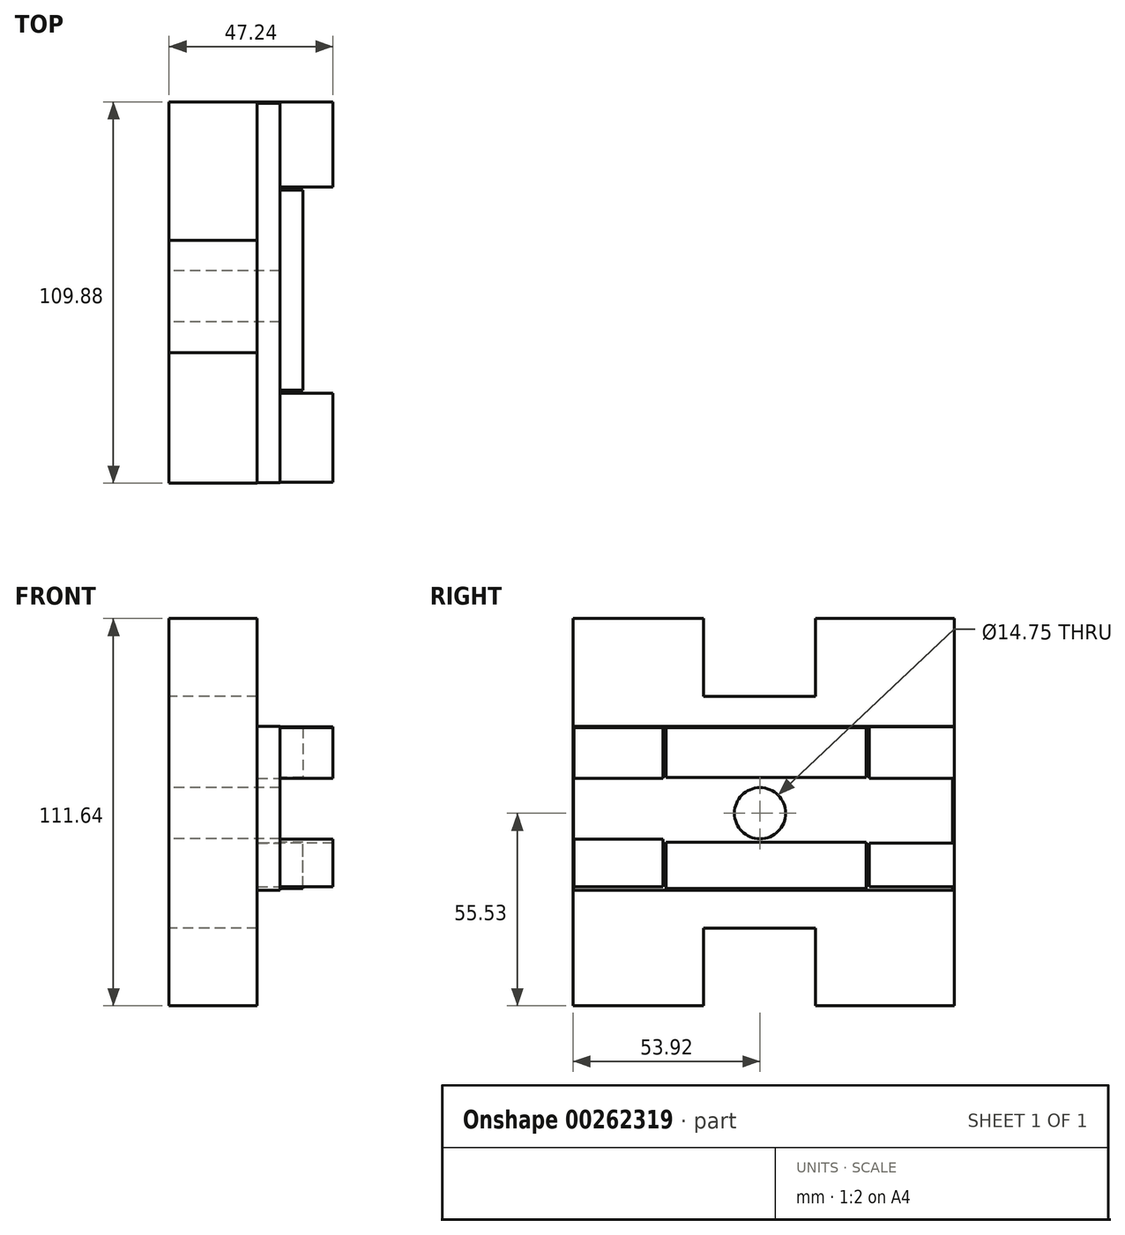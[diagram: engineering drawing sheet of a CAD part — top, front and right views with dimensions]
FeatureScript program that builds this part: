
annotation { "Feature Type Name" : "Feature", "Feature Type Description" : "" }
export const myFeature = defineFeature(function(context is Context, id is Id, definition is map)
    precondition{}
    {
        {
            var Q0;
            Q0=qCreatedBy(makeId("Right.planeOp"),FACE);
            var sketch = newSketch(context, id + "F0", { "sketchPlane" : qUnion([Q0])});
            skLineSegment(sketch, "E0.bottom", {"start": v(-53.92, 56.1) * mm, "end": v(55.96, 56.1) * mm});
            skLineSegment(sketch, "E0.top", {"start": v(-53.92, -55.53) * mm, "end": v(55.96, -55.53) * mm});
            skLineSegment(sketch, "E0.left", {"start": v(-53.92, 56.1) * mm, "end": v(-53.92, -55.53) * mm});
            skLineSegment(sketch, "E0.right", {"start": v(55.96, 56.1) * mm, "end": v(55.96, -55.53) * mm});
            skLineSegment(sketch, "E1.bottom", {"start": v(-16.32, 56.1) * mm, "end": v(16.03, 56.1) * mm});
            skLineSegment(sketch, "E1.top", {"start": v(-16.32, 33.67) * mm, "end": v(16.03, 33.67) * mm});
            skLineSegment(sketch, "E1.left", {"start": v(-16.32, 56.1) * mm, "end": v(-16.32, 33.67) * mm});
            skLineSegment(sketch, "E1.right", {"start": v(16.03, 56.1) * mm, "end": v(16.03, 33.67) * mm});
            skLineSegment(sketch, "E2.bottom", {"start": v(-16.32, -55.53) * mm, "end": v(16.03, -55.53) * mm});
            skLineSegment(sketch, "E2.top", {"start": v(-16.32, -33.08) * mm, "end": v(16.03, -33.08) * mm});
            skLineSegment(sketch, "E2.left", {"start": v(-16.32, -55.53) * mm, "end": v(-16.32, -33.08) * mm});
            skLineSegment(sketch, "E2.right", {"start": v(16.03, -55.53) * mm, "end": v(16.03, -33.08) * mm});
            skSolve(sketch);
        }
        {
            var Q0;
            {var subQ0=sQuery(id+"F0.wireOp",EDGE,"E0.left");Q0=makeQuery(id+"F0.imprint","IMPRINT",FACE,{"disambiguationData":[TD([[makeQuery(id+"F0.imprint","IMPRINT",EDGE,{"derivedFrom":subQ0}),1.0]])]});}
            extrude(context, id + "F1", {"entities" : qUnion([Q0]), "depth" : 25.4 * mm});
        }
        {
            var Q0;
            Q0=qCreatedBy(makeId("Right.planeOp"),FACE);
            var sketch = newSketch(context, id + "F2", { "sketchPlane" : qUnion([Q0])});
            skLineSegment(sketch, "E3", {"start": v(55.53, 25.07) * mm, "end": v(-53.78, 25.07) * mm});
            skLineSegment(sketch, "E4", {"start": v(-53.78, 25.07) * mm, "end": v(-53.78, -22.15) * mm});
            skLineSegment(sketch, "E5", {"start": v(-53.78, -22.15) * mm, "end": v(55.53, -22.15) * mm});
            skLineSegment(sketch, "E6", {"start": v(55.53, -22.15) * mm, "end": v(55.53, 25.07) * mm});
            skSolve(sketch);
        }
        {
            var Q0;
            Q0 = qSketchRegion(id + "F2", true);
            extrude(context, id + "F3", {"entities" : qUnion([Q0]), "operationType" : NewBodyOperationType.ADD, "depth" : 32 * mm});
        }
        {
            var Q0;
            Q0=qCreatedBy(makeId("Right.planeOp"),FACE);
            var sketch = newSketch(context, id + "F4", { "sketchPlane" : qUnion([Q0])});
            skLineSegment(sketch, "E7", {"start": v(-53.63, 10.06) * mm, "end": v(-27.98, 10.06) * mm});
            skLineSegment(sketch, "E8", {"start": v(-27.98, 24.63) * mm, "end": v(-27.98, 10.06) * mm});
            skLineSegment(sketch, "E9", {"start": v(-53.63, -21.13) * mm, "end": v(-53.63, -7.43) * mm});
            skLineSegment(sketch, "E10", {"start": v(-53.63, -7.43) * mm, "end": v(-27.98, -7.43) * mm});
            skLineSegment(sketch, "E11", {"start": v(-27.98, -7.43) * mm, "end": v(-27.98, -21.13) * mm});
            skLineSegment(sketch, "E12", {"start": v(-27.98, -21.13) * mm, "end": v(-53.63, -21.13) * mm});
            skLineSegment(sketch, "E13", {"start": v(-53.63, -7.43) * mm, "end": v(-53.63, -21.13) * mm});
            skLineSegment(sketch, "E14", {"start": v(-53.63, 10.06) * mm, "end": v(-53.63, 24.63) * mm});
            skLineSegment(sketch, "E15", {"start": v(-53.63, 24.63) * mm, "end": v(-27.98, 24.63) * mm});
            skLineSegment(sketch, "E16.bottom", {"start": v(55.67, 10.06) * mm, "end": v(31.48, 10.06) * mm});
            skLineSegment(sketch, "E16.top", {"start": v(55.67, 10.06) * mm, "end": v(31.48, 10.06) * mm});
            skLineSegment(sketch, "E16.left", {"start": v(55.67, 10.06) * mm, "end": v(55.67, 10.06) * mm});
            skLineSegment(sketch, "E16.right", {"start": v(31.48, 10.06) * mm, "end": v(31.48, 10.06) * mm});
            skLineSegment(sketch, "E17.bottom", {"start": v(31.48, 24.92) * mm, "end": v(31.48, 24.92) * mm});
            skLineSegment(sketch, "E17.left", {"start": v(31.48, 24.92) * mm, "end": v(31.48, 10.06) * mm});
            skLineSegment(sketch, "E17.right", {"start": v(31.48, 24.92) * mm, "end": v(31.48, 10.06) * mm});
            skLineSegment(sketch, "E18.bottom", {"start": v(31.48, 24.92) * mm, "end": v(55.96, 24.92) * mm});
            skLineSegment(sketch, "E18.top", {"start": v(31.48, 24.92) * mm, "end": v(55.96, 24.92) * mm});
            skLineSegment(sketch, "E18.right", {"start": v(55.96, 24.92) * mm, "end": v(55.96, 24.92) * mm});
            skLineSegment(sketch, "E19.bottom", {"start": v(55.67, 10.06) * mm, "end": v(55.96, 10.06) * mm});
            skLineSegment(sketch, "E19.top", {"start": v(55.67, 24.92) * mm, "end": v(55.96, 24.92) * mm});
            skLineSegment(sketch, "E19.left", {"start": v(55.67, 10.06) * mm, "end": v(55.67, 24.92) * mm});
            skLineSegment(sketch, "E19.right", {"start": v(55.96, 10.06) * mm, "end": v(55.96, 24.92) * mm});
            skLineSegment(sketch, "E20.bottom", {"start": v(55.96, -21.13) * mm, "end": v(31.48, -21.13) * mm});
            skLineSegment(sketch, "E20.top", {"start": v(55.96, -8.6) * mm, "end": v(31.48, -8.6) * mm});
            skLineSegment(sketch, "E20.left", {"start": v(55.96, -21.13) * mm, "end": v(55.96, -8.6) * mm});
            skLineSegment(sketch, "E20.right", {"start": v(31.48, -21.13) * mm, "end": v(31.48, -8.6) * mm});
            skSolve(sketch);
        }
        {
            var Q0;
            Q0 = qSketchRegion(id + "F4", true);
            extrude(context, id + "F5", {"entities" : qUnion([Q0]), "operationType" : NewBodyOperationType.ADD, "depth" : 47.24 * mm});
        }
        {
            var Q0;
            Q0=qCreatedBy(makeId("Right.planeOp"),FACE);
            var sketch = newSketch(context, id + "F6", { "sketchPlane" : qUnion([Q0])});
            skLineSegment(sketch, "E21.bottom", {"start": v(-27.1, 24.63) * mm, "end": v(30.6, 24.63) * mm});
            skLineSegment(sketch, "E21.top", {"start": v(-27.1, 10.35) * mm, "end": v(30.6, 10.35) * mm});
            skLineSegment(sketch, "E21.left", {"start": v(-27.1, 24.63) * mm, "end": v(-27.1, 10.35) * mm});
            skLineSegment(sketch, "E21.right", {"start": v(30.6, 24.63) * mm, "end": v(30.6, 10.35) * mm});
            skLineSegment(sketch, "E22.bottom", {"start": v(30.6, -21.71) * mm, "end": v(-27.1, -21.71) * mm});
            skLineSegment(sketch, "E22.top", {"start": v(30.6, -8.3) * mm, "end": v(-27.1, -8.3) * mm});
            skLineSegment(sketch, "E22.left", {"start": v(30.6, -21.71) * mm, "end": v(30.6, -8.3) * mm});
            skLineSegment(sketch, "E22.right", {"start": v(-27.1, -21.71) * mm, "end": v(-27.1, -8.3) * mm});
            skSolve(sketch);
        }
        {
            var Q0;
            Q0 = qSketchRegion(id + "F6", true);
            extrude(context, id + "F7", {"entities" : qUnion([Q0]), "operationType" : NewBodyOperationType.ADD, "depth" : 38.6 * mm});
        }
        {
            var Q0;
            Q0=qCreatedBy(makeId("Right.planeOp"),FACE);
            var sketch = newSketch(context, id + "F8", { "sketchPlane" : qUnion([Q0])});
            skCircle(sketch, "E23", {"center": v(0, 0) * mm, "radius": 7.38 * mm});
            skSolve(sketch);
        }
        {
            var Q0;
            Q0 = qSketchRegion(id + "F8", true);
            extrude(context, id + "F9", {"entities" : qUnion([Q0]), "operationType" : NewBodyOperationType.REMOVE, "depth" : 65.28 * mm});
        }
    });
